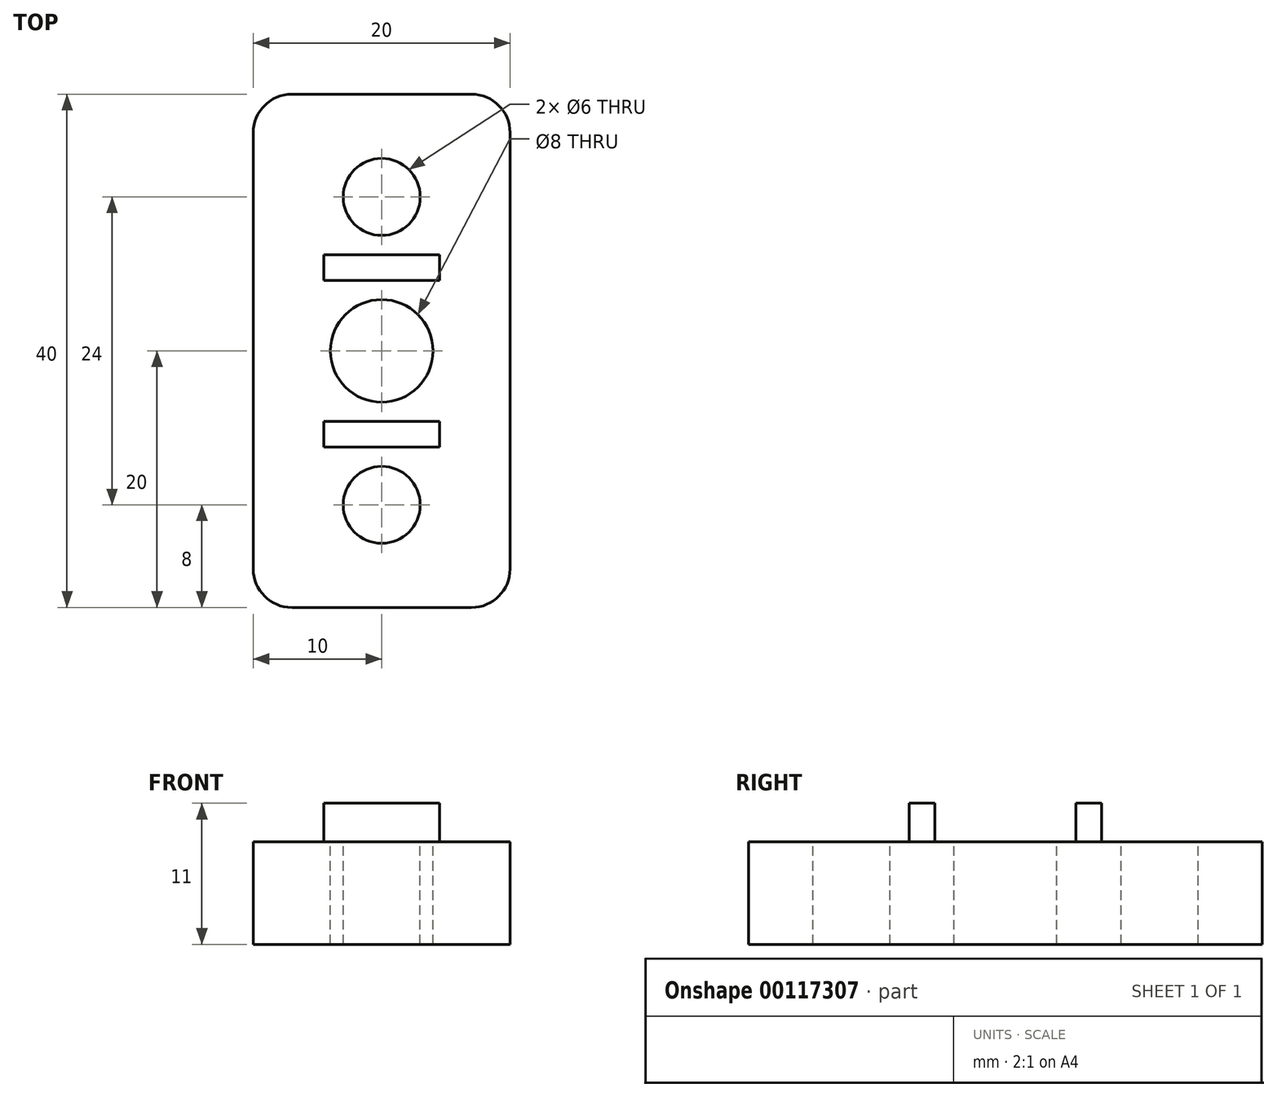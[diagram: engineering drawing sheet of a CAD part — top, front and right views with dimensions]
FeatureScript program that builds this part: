
annotation { "Feature Type Name" : "Feature", "Feature Type Description" : "" }
export const myFeature = defineFeature(function(context is Context, id is Id, definition is map)
    precondition{}
    {
        {
            var Q0;
            Q0=qCreatedBy(makeId("Top.planeOp"),FACE);
            var sketch = newSketch(context, id + "F0", { "sketchPlane" : qUnion([Q0])});
            skLineSegment(sketch, "E0.bottom", {"start": v(-7, 20) * mm, "end": v(7, 20) * mm});
            skLineSegment(sketch, "E0.top", {"start": v(-7, -20) * mm, "end": v(7, -20) * mm});
            skLineSegment(sketch, "E0.left", {"start": v(-10, 17) * mm, "end": v(-10, -17) * mm});
            skLineSegment(sketch, "E0.right", {"start": v(10, 17) * mm, "end": v(10, -17) * mm});
            skPoint(sketch, "E1.visualSharp", {"position": v(-10, 20) * mm});
            skArc(sketch, "E1.filletArc", {"start": v(-7, 20) * mm, "mid": v(-9.12, 19.12) * mm, "end": v(-10, 17) * mm});
            skPoint(sketch, "E2.visualSharp", {"position": v(10, 20) * mm});
            skArc(sketch, "E2.filletArc", {"start": v(10, 17) * mm, "mid": v(9.12, 19.12) * mm, "end": v(7, 20) * mm});
            skPoint(sketch, "E3.visualSharp", {"position": v(10, -20) * mm});
            skArc(sketch, "E3.filletArc", {"start": v(7, -20) * mm, "mid": v(9.12, -19.12) * mm, "end": v(10, -17) * mm});
            skPoint(sketch, "E4.visualSharp", {"position": v(-10, -20) * mm});
            skArc(sketch, "E4.filletArc", {"start": v(-10, -17) * mm, "mid": v(-9.12, -19.12) * mm, "end": v(-7, -20) * mm});
            skSolve(sketch);
        }
        {
            var Q0;
            Q0 = qSketchRegion(id + "F0", true);
            extrude(context, id + "F1", {"entities" : qUnion([Q0]), "depth" : 8 * mm});
        }
        {
            var Q0;
            Q0=makeQuery(id+"F1.opExtrude","CAP_FACE",FACE,{"disambiguationData":[OSD([sQuery(id+"F0.wireOp",EDGE,"E0.bottom"),sQuery(id+"F0.wireOp",EDGE,"E0.top"),sQuery(id+"F0.wireOp",EDGE,"E0.left"),sQuery(id+"F0.wireOp",EDGE,"E0.right"),sQuery(id+"F0.wireOp",EDGE,"E1.filletArc"),sQuery(id+"F0.wireOp",EDGE,"E2.filletArc"),sQuery(id+"F0.wireOp",EDGE,"E3.filletArc"),sQuery(id+"F0.wireOp",EDGE,"E4.filletArc")])],"isStart":false});
            var sketch = newSketch(context, id + "F2", { "sketchPlane" : qUnion([Q0])});
            skCircle(sketch, "E5", {"center": v(0, 12) * mm, "radius": 3 * mm});
            skCircle(sketch, "E6", {"center": v(0, -12) * mm, "radius": 3 * mm});
            skSolve(sketch);
        }
        {
            var Q0;
            Q0 = qSketchRegion(id + "F2", true);
            extrude(context, id + "F3", {"entities" : qUnion([Q0]), "operationType" : NewBodyOperationType.REMOVE, "endBound" : BoundingType.UP_TO_NEXT, "oppositeDirection" : true, "depth" : 25 * mm});
        }
        {
            var Q0;
            Q0=makeQuery(id+"F1.opExtrude","CAP_FACE",FACE,{"disambiguationData":[OSD([sQuery(id+"F0.wireOp",EDGE,"E0.bottom"),sQuery(id+"F0.wireOp",EDGE,"E0.top"),sQuery(id+"F0.wireOp",EDGE,"E0.left"),sQuery(id+"F0.wireOp",EDGE,"E0.right"),sQuery(id+"F0.wireOp",EDGE,"E1.filletArc"),sQuery(id+"F0.wireOp",EDGE,"E2.filletArc"),sQuery(id+"F0.wireOp",EDGE,"E3.filletArc"),sQuery(id+"F0.wireOp",EDGE,"E4.filletArc")])],"isStart":false});
            var sketch = newSketch(context, id + "F4", { "sketchPlane" : qUnion([Q0])});
            skCircle(sketch, "E7", {"center": v(0, 0) * mm, "radius": 4 * mm});
            skSolve(sketch);
        }
        {
            var Q0;
            Q0 = qSketchRegion(id + "F4", true);
            extrude(context, id + "F5", {"entities" : qUnion([Q0]), "operationType" : NewBodyOperationType.REMOVE, "endBound" : BoundingType.UP_TO_NEXT, "oppositeDirection" : true, "depth" : 4 * mm});
        }
        {
            var Q0;
            Q0=makeQuery(id+"F1.opExtrude","CAP_FACE",FACE,{"disambiguationData":[OSD([sQuery(id+"F0.wireOp",EDGE,"E0.bottom"),sQuery(id+"F0.wireOp",EDGE,"E0.top"),sQuery(id+"F0.wireOp",EDGE,"E0.left"),sQuery(id+"F0.wireOp",EDGE,"E0.right"),sQuery(id+"F0.wireOp",EDGE,"E1.filletArc"),sQuery(id+"F0.wireOp",EDGE,"E2.filletArc"),sQuery(id+"F0.wireOp",EDGE,"E3.filletArc"),sQuery(id+"F0.wireOp",EDGE,"E4.filletArc")])],"isStart":false});
            var sketch = newSketch(context, id + "F6", { "sketchPlane" : qUnion([Q0])});
            skLineSegment(sketch, "E8.bottom", {"start": v(-4.5, -5.5) * mm, "end": v(4.5, -5.5) * mm});
            skLineSegment(sketch, "E8.top", {"start": v(-4.5, -7.5) * mm, "end": v(4.5, -7.5) * mm});
            skLineSegment(sketch, "E8.left", {"start": v(-4.5, -5.5) * mm, "end": v(-4.5, -7.5) * mm});
            skLineSegment(sketch, "E8.right", {"start": v(4.5, -5.5) * mm, "end": v(4.5, -7.5) * mm});
            skLineSegment(sketch, "E9.bottom", {"start": v(-4.5, 7.5) * mm, "end": v(4.5, 7.5) * mm});
            skLineSegment(sketch, "E9.top", {"start": v(-4.5, 5.5) * mm, "end": v(4.5, 5.5) * mm});
            skLineSegment(sketch, "E9.left", {"start": v(-4.5, 7.5) * mm, "end": v(-4.5, 5.5) * mm});
            skLineSegment(sketch, "E9.right", {"start": v(4.5, 7.5) * mm, "end": v(4.5, 5.5) * mm});
            skSolve(sketch);
        }
        {
            var Q0;
            Q0 = qSketchRegion(id + "F6", true);
            extrude(context, id + "F7", {"entities" : qUnion([Q0]), "operationType" : NewBodyOperationType.ADD, "depth" : 3 * mm});
        }
    });
